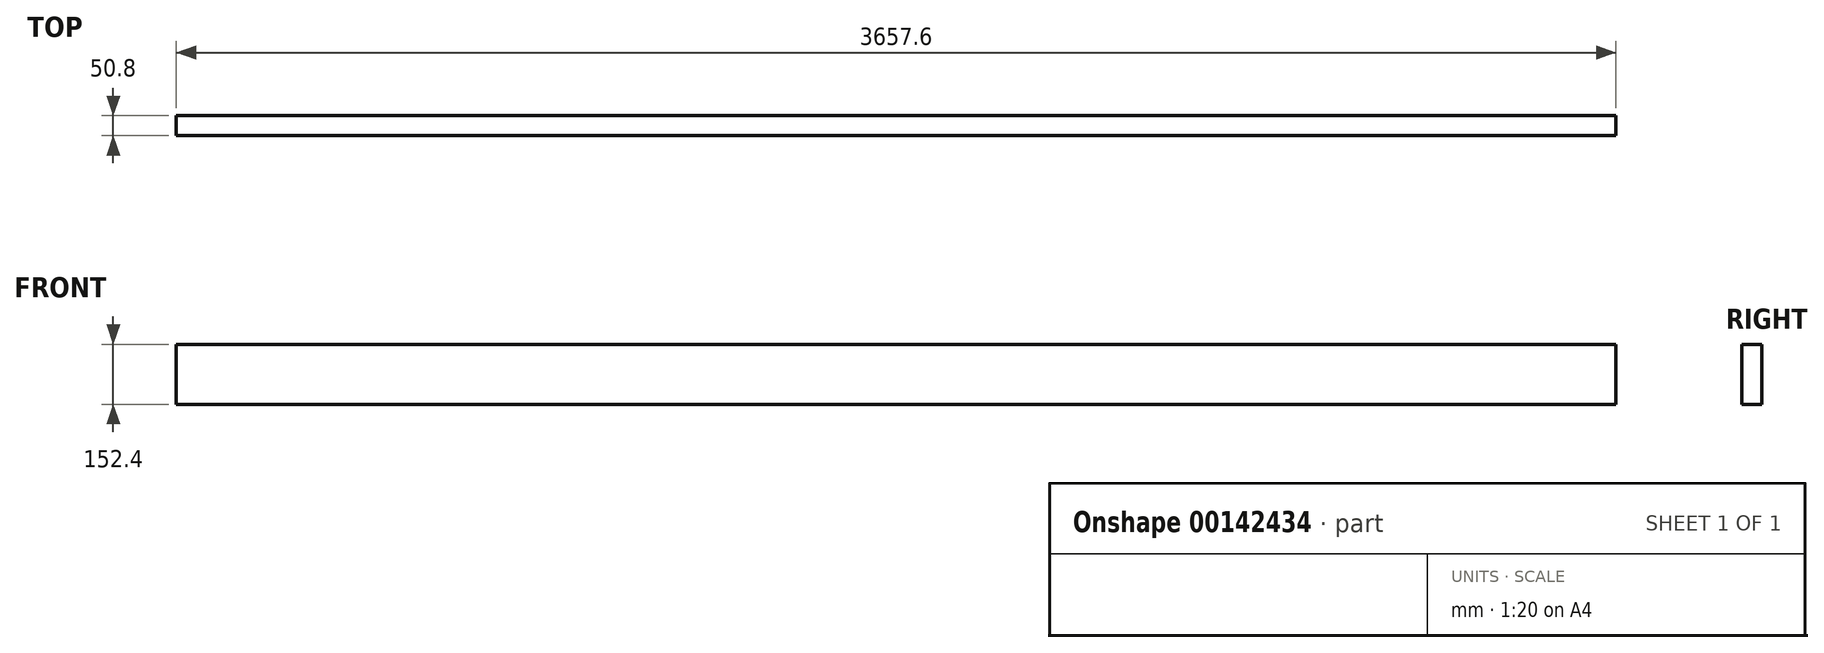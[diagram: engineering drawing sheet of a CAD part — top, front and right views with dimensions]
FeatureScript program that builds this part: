
annotation { "Feature Type Name" : "Feature", "Feature Type Description" : "" }
export const myFeature = defineFeature(function(context is Context, id is Id, definition is map)
    precondition{}
    {
        {
            var Q0;
            Q0=qCreatedBy(makeId("Front.planeOp"),FACE);
            var sketch = newSketch(context, id + "F0", { "sketchPlane" : qUnion([Q0])});
            skLineSegment(sketch, "E0.bottom", {"start": v(1828.8, 76.2) * mm, "end": v(-1828.8, 76.2) * mm});
            skLineSegment(sketch, "E0.top", {"start": v(1828.8, -76.2) * mm, "end": v(-1828.8, -76.2) * mm});
            skLineSegment(sketch, "E0.left", {"start": v(1828.8, 76.2) * mm, "end": v(1828.8, -76.2) * mm});
            skLineSegment(sketch, "E0.right", {"start": v(-1828.8, 76.2) * mm, "end": v(-1828.8, -76.2) * mm});
            skPoint(sketch, "E0.middle", {"position": v(0, 0) * mm});
            skSolve(sketch);
        }
        {
            var Q0;
            Q0=makeQuery(id+"F0.imprint","IMPRINT",FACE,{"disambiguationData":[TD([[makeQuery(id+"F0.imprint","IMPRINT",EDGE,{"derivedFrom":sQuery(id+"F0.wireOp",EDGE,"E0.bottom")}),1.0]])]});
            extrude(context, id + "F1", {"entities" : qUnion([Q0]), "endBound" : BoundingType.SYMMETRIC, "depth" : 50.8 * mm});
        }
    });
